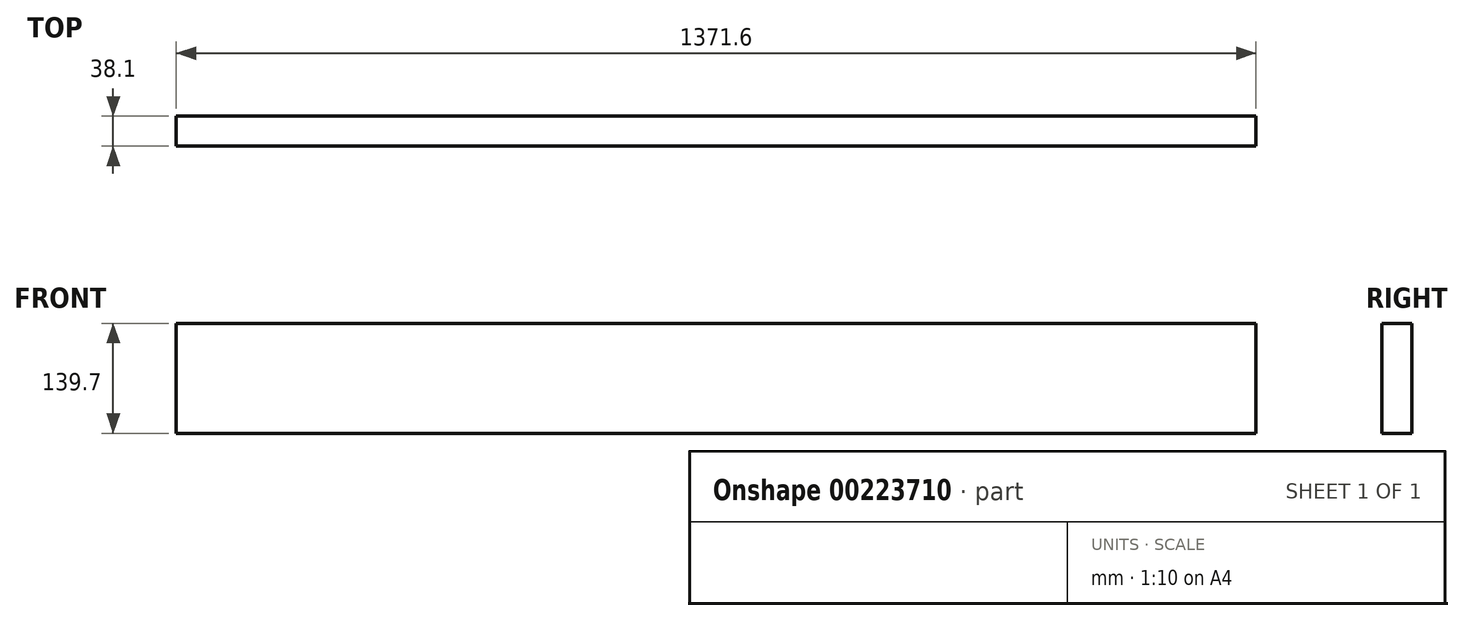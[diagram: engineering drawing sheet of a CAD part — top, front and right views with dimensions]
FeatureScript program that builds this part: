
annotation { "Feature Type Name" : "Feature", "Feature Type Description" : "" }
export const myFeature = defineFeature(function(context is Context, id is Id, definition is map)
    precondition{}
    {
        {
            var Q0;
            Q0=qCreatedBy(makeId("Front.planeOp"),FACE);
            var sketch = newSketch(context, id + "F0", { "sketchPlane" : qUnion([Q0])});
            skLineSegment(sketch, "E0.bottom", {"start": v(-685.24, 41.6) * mm, "end": v(686.36, 41.6) * mm});
            skLineSegment(sketch, "E0.top", {"start": v(-685.24, -98.1) * mm, "end": v(686.36, -98.1) * mm});
            skLineSegment(sketch, "E0.left", {"start": v(-685.24, 41.6) * mm, "end": v(-685.24, -98.1) * mm});
            skLineSegment(sketch, "E0.right", {"start": v(686.36, 41.6) * mm, "end": v(686.36, -98.1) * mm});
            skSolve(sketch);
        }
        {
            var Q0;
            Q0=makeQuery(id+"F0.imprint","IMPRINT",FACE,{"disambiguationData":[TD([[makeQuery(id+"F0.imprint","IMPRINT",EDGE,{"derivedFrom":sQuery(id+"F0.wireOp",EDGE,"E0.bottom")}),-1.0]])]});
            extrude(context, id + "F1", {"entities" : qUnion([Q0]), "depth" : 38.1 * mm});
        }
    });
